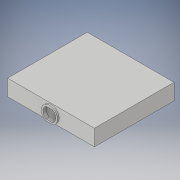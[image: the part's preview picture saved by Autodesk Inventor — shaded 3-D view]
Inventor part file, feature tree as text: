
AUTODESK INVENTOR PART (.ipt)
format: ipt  version: 2017 (Build 210142000, 142)  size: 347,648 bytes
history: native  units: in
note: dims shown in document units (in); Inventor stores cm internally (conversion verified against a paired STEP export)
features: extrude x7, sketch x6
ambient origin geometry x8: Origin, YZ Plane, XZ Plane, XY Plane, X Axis, Y Axis, Z Axis, Center Point
bodies: Solid1 (feature_tree), Solid2 (feature_tree)
feature tree (13):
  extrude  "cubicals"  Depth=12.0in
  extrude  "floor"  Depth=2.5in
  extrude  "walls"  Depth=0.0833in
  sketch  "Sketch4"  dims[d10=0.0833in d95=0.0833in]
  extrude  "connection"  Depth=0.0833in
  extrude  "light connection"  Depth=2.5in
  extrude  "connection cut"  Depth=2.5in
  extrude  "Extrusion8"  Depth=1.0in
  sketch  "Sketch2"  dims[d2=4.5in d3=0.0in d4=12.0in]
  sketch  "Sketch3"  dims[d5=8.0in d7=2.5in]
  sketch  "Sketch5"  dims[d97=0.0833in d98=0.0833in]
  sketch  "Sketch6"  dims[d99=12.0in d100=8.0in d102=0.0833in d103=0.0833in d104=0.0833in d105=0.0833in]
  sketch  "Sketch7"  dims[d106=12.0in d107=8.0in d109=0.0833in d110=0.0833in d111=0.0833in d112=0.0833in d113=2.5in d114=2.5in d115=3.0in d117=3.0in d118=6.0in d120=6.0in d121=1.0in d122=0.0in d128=1.0in d129=1.0in d130=1.0in d131=1.0in d132=1.0in d133=1.0in d134=7.7746in d135=0.0in d148=4.0in d149=1.0in d150=4.8944in d151=0.5833in d152=3.8873in d153=3.8873in d154=1.7083in d155=0.0625in d156=0.0625in d157=1.6458in d158=0.125in d159=0.125in d160=1.0in d161=0.0in d164=0.25in d165=0.125in d166=45.0deg d167=0.0892in d168=0.0884in d169=1.0in d170=0.0in d171=1.0in d172=0.0in d173=1.0in d174=0.0in]
